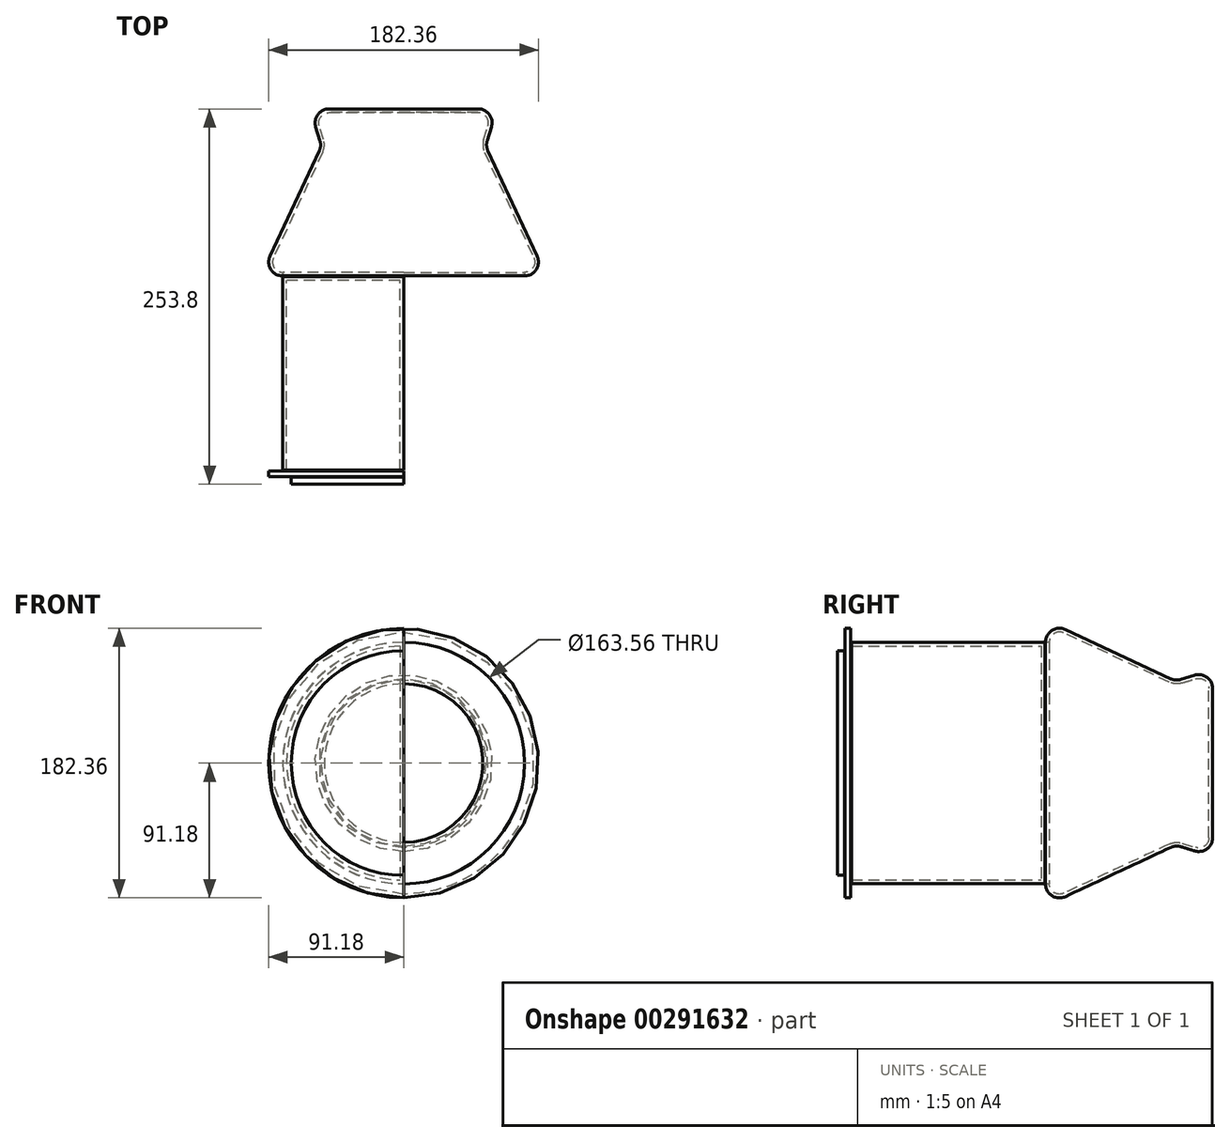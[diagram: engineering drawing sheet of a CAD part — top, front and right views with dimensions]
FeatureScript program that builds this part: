
annotation { "Feature Type Name" : "Feature", "Feature Type Description" : "" }
export const myFeature = defineFeature(function(context is Context, id is Id, definition is map)
    precondition{}
    {
        {
            var Q0;
            Q0=qCreatedBy(makeId("Front.planeOp"),FACE);
            var sketch = newSketch(context, id + "F0", { "sketchPlane" : qUnion([Q0])});
            skCircle(sketch, "E0", {"center": v(0, 0) * mm, "radius": 55.5 * mm});
            skSolve(sketch);
        }
        {
            var Q0;
            Q0=makeQuery(id+"F0.imprint","IMPRINT",FACE,{"disambiguationData":[TD([[makeQuery(id+"F0.imprint","IMPRINT",EDGE,{"derivedFrom":sQuery(id+"F0.wireOp",EDGE,"E0")}),1.0]])]});
            extrude(context, id + "F1", {"entities" : qUnion([Q0]), "depth" : 88 * mm, "hasDraft" : true, "draftAngle" : 25 * degree, "hasSecondDirection" : true, "secondDirectionOppositeDirection" : true, "secondDirectionDepth" : 25 * mm, "hasSecondDirectionDraft" : true, "secondDirectionDraftAngle" : 17 * degree});
        }
        {
            var Q0;
            Q0=makeQuery(id+"F1.opExtrude","CAP_FACE",FACE,{"disambiguationData":[OSD([sQuery(id+"F0.wireOp",EDGE,"E0")])],"isStart":false});
            var Q1;
            Q1=makeQuery(id+"F1.*.split.splitOp","SPLIT",FACE,{"derivedFrom":makeQuery(id+"F1.opExtrude","SWEPT_FACE",FACE,{"disambiguationData":[OSD([sQuery(id+"F0.wireOp",EDGE,"E0")])]}),"isFromBackBody":true});
            fillet(context, id + "F2", {"entities" : qUnion([Q0, Q1]), "radius" : 9.4 * mm, "tangentPropagation" : true, "allowEdgeOverflow" : false});
        }
        {
            var Q0;
            Q0=makeQuery(id+"F1.opExtrude","CAP_FACE",FACE,{"disambiguationData":[OSD([sQuery(id+"F0.wireOp",EDGE,"E0")])],"isStart":false});
            cPlane(context, id + "F3", {"entities" : qUnion([Q0]), "cplaneType" : CPlaneType.OFFSET, "offset" : 0.4 * mm, "width" : 150 * mm, "height" : 150 * mm});
        }
        {
            var Q0;
            Q0=qCreatedBy(id+"F3.planeOp",FACE);
            var sketch = newSketch(context, id + "F4", { "sketchPlane" : qUnion([Q0])});
            skArc(sketch, "E1", {"start": v(0, 81.65) * mm, "mid": v(-81.65, 0) * mm, "end": v(0, -81.65) * mm});
            skLineSegment(sketch, "E2", {"start": v(0, 81.65) * mm, "end": v(0, -81.65) * mm});
            skSolve(sketch);
        }
        {
            var Q0;
            Q0=makeQuery(id+"F4.imprint","IMPRINT",FACE,{"disambiguationData":[TD([[makeQuery(id+"F4.imprint","IMPRINT",EDGE,{"derivedFrom":sQuery(id+"F4.wireOp",EDGE,"E1")}),1.0]])]});
            extrude(context, id + "F5", {"entities" : qUnion([Q0]), "depth" : 131 * mm});
        }
        {
            var Q0;
            Q0=makeQuery(id+"F1.opExtrude","CAP_FACE",FACE,{"disambiguationData":[OSD([sQuery(id+"F0.wireOp",EDGE,"E0")])],"isStart":false});
            shell(context, id + "F6", {"entities" : qUnion([Q0]), "thickness" : 2.5 * mm});
        }
        {
            var Q0;
            Q0=makeQuery(id+"F5.opExtrude","CAP_FACE",FACE,{"disambiguationData":[OSD([sQuery(id+"F4.wireOp",EDGE,"E1"),sQuery(id+"F4.wireOp",EDGE,"E2")])],"isStart":false});
            shell(context, id + "F7", {"entities" : qUnion([Q0]), "thickness" : 2.5 * mm});
        }
        {
            var Q0;
            Q0=qCreatedBy(id+"F3.planeOp",FACE);
            cPlane(context, id + "F8", {"entities" : qUnion([Q0]), "cplaneType" : CPlaneType.OFFSET, "offset" : 131.6 * mm, "width" : 150 * mm, "height" : 150 * mm});
        }
        {
            var Q0;
            Q0=qCreatedBy(id+"F8.planeOp",FACE);
            var sketch = newSketch(context, id + "F9", { "sketchPlane" : qUnion([Q0])});
            skPoint(sketch, "E3.start.orphan", {"position": v(0, 82.1) * mm});
            skArc(sketch, "E4", {"start": v(0, 91.14) * mm, "mid": v(-91.14, 0) * mm, "end": v(0, -91.14) * mm});
            skLineSegment(sketch, "E5", {"start": v(0, 91.14) * mm, "end": v(0, -91.14) * mm});
            skSolve(sketch);
        }
        {
            var Q0;
            Q0=makeQuery(id+"F9.imprint","IMPRINT",FACE,{"disambiguationData":[TD([[makeQuery(id+"F9.imprint","IMPRINT",EDGE,{"derivedFrom":sQuery(id+"F9.wireOp",EDGE,"E4")}),1.0]])]});
            extrude(context, id + "F10", {"entities" : qUnion([Q0]), "depth" : 3.6 * mm});
        }
        {
            var Q0;
            Q0=qCreatedBy(id+"F8.planeOp",FACE);
            cPlane(context, id + "F11", {"entities" : qUnion([Q0]), "cplaneType" : CPlaneType.OFFSET, "offset" : 4.1 * mm, "width" : 150 * mm, "height" : 150 * mm});
        }
        {
            var Q0;
            Q0=qCreatedBy(id+"F11.planeOp",FACE);
            var sketch = newSketch(context, id + "F12", { "sketchPlane" : qUnion([Q0])});
            skArc(sketch, "E6", {"start": v(0, 75.97) * mm, "mid": v(-75.97, 0) * mm, "end": v(0, -75.97) * mm});
            skLineSegment(sketch, "E7", {"start": v(0, 75.97) * mm, "end": v(0, -75.97) * mm});
            skSolve(sketch);
        }
        {
            var Q0;
            Q0=makeQuery(id+"F12.imprint","IMPRINT",FACE,{"disambiguationData":[TD([[makeQuery(id+"F12.imprint","IMPRINT",EDGE,{"derivedFrom":sQuery(id+"F12.wireOp",EDGE,"E6")}),1.0]])]});
            extrude(context, id + "F13", {"entities" : qUnion([Q0]), "depth" : 4.7 * mm});
        }
    });
